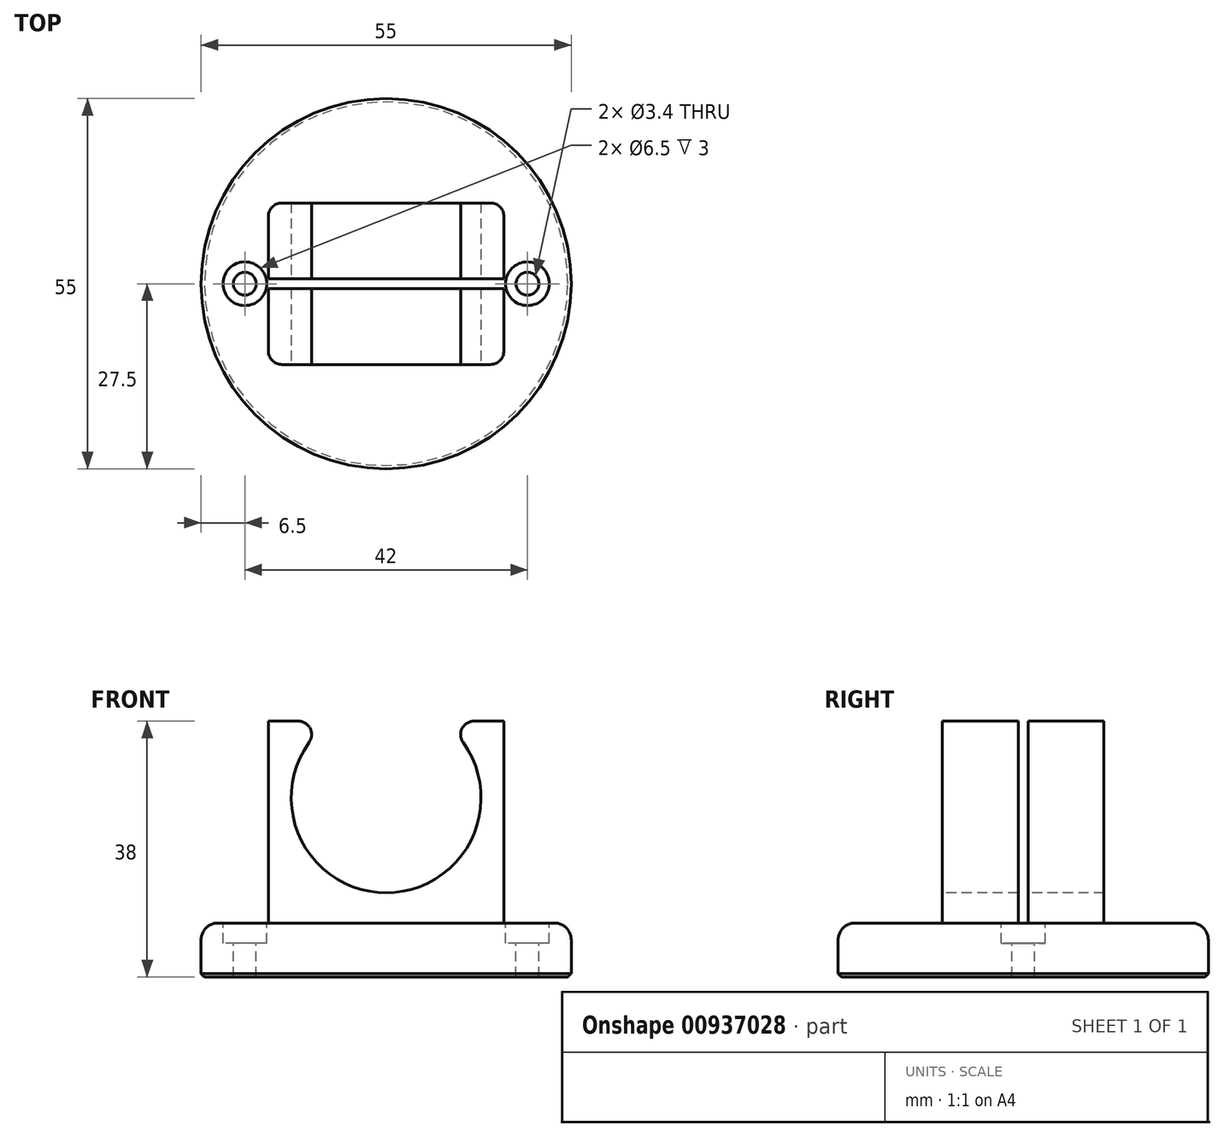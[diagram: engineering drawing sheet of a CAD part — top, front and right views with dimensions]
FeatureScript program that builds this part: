
annotation { "Feature Type Name" : "Feature", "Feature Type Description" : "" }
export const myFeature = defineFeature(function(context is Context, id is Id, definition is map)
    precondition{}
    {
        {
            var Q0;
            Q0=qCreatedBy(makeId("Top.planeOp"),FACE);
            var sketch = newSketch(context, id + "F0", { "sketchPlane" : qUnion([Q0])});
            skCircle(sketch, "E0", {"center": v(0, 0) * mm, "radius": 27.5 * mm});
            skSolve(sketch);
        }
        {
            var Q0;
            Q0 = qSketchRegion(id + "F0", true);
            extrude(context, id + "F1", {"entities" : qUnion([Q0]), "depth" : 8 * mm, "offsetDistance" : 25 * mm});
        }
        {
            var Q0;
            Q0=makeQuery(id+"F1.opExtrude","CAP_FACE",FACE,{"disambiguationData":[OSD([sQuery(id+"F0.wireOp",EDGE,"E0")])],"isStart":false});
            var sketch = newSketch(context, id + "F2", { "sketchPlane" : qUnion([Q0])});
            skLineSegment(sketch, "E1.bottom", {"start": v(17.5, -12) * mm, "end": v(-17.5, -12) * mm});
            skLineSegment(sketch, "E1.top", {"start": v(17.5, 12) * mm, "end": v(-17.5, 12) * mm});
            skLineSegment(sketch, "E1.left", {"start": v(17.5, -12) * mm, "end": v(17.5, 12) * mm});
            skLineSegment(sketch, "E1.right", {"start": v(-17.5, -12) * mm, "end": v(-17.5, 12) * mm});
            skPoint(sketch, "E1.middle", {"position": v(0, 0) * mm});
            skSolve(sketch);
        }
        {
            var Q0;
            Q0 = qSketchRegion(id + "F2", true);
            extrude(context, id + "F3", {"entities" : qUnion([Q0]), "operationType" : NewBodyOperationType.ADD, "depth" : 30 * mm, "offsetDistance" : 25 * mm});
        }
        {
            var Q0;
            Q0=makeQuery(id+"F1.opExtrude","CAP_FACE",FACE,{"disambiguationData":[OSD([sQuery(id+"F0.wireOp",EDGE,"E0")])],"isStart":false});
            var sketch = newSketch(context, id + "F4", { "sketchPlane" : qUnion([Q0])});
            skPoint(sketch, "E2", {"position": v(21, 0) * mm});
            skPoint(sketch, "E3", {"position": v(-21, 0) * mm});
            skSolve(sketch);
        }
        {
            var Q0;
            Q0=makeQuery(id+"F3.opExtrude","SWEPT_FACE",FACE,{"disambiguationData":[OSD([sQuery(id+"F2.wireOp",EDGE,"E1.bottom")])]});
            var sketch = newSketch(context, id + "F5", { "sketchPlane" : qUnion([Q0])});
            skArc(sketch, "E4", {"start": v(-8.2, 38.07) * mm, "mid": v(0, 12.5) * mm, "end": v(8.2, 38.07) * mm});
            skLineSegment(sketch, "E5", {"start": v(-8.2, 38.07) * mm, "end": v(8.2, 38.07) * mm});
            skSolve(sketch);
        }
        {
            var Q0;
            Q0 = qSketchRegion(id + "F5", true);
            extrude(context, id + "F6", {"entities" : qUnion([Q0]), "operationType" : NewBodyOperationType.REMOVE, "oppositeDirection" : true, "depth" : 24 * mm, "offsetDistance" : 25 * mm});
        }
        {
            var Q0;
            Q0=makeQuery(id+"F6.boolean.opBoolean","COPY",EDGE,{"derivedFrom":makeQuery(id+"F6.opExtrude","CAP_EDGE",EDGE,{"disambiguationData":[OSD([sQuery(id+"F5.wireOp",EDGE,"E4")])],"isStart":true})});
            var Q1;
            Q1=makeQuery(id+"F6.boolean.opBoolean","COPY",EDGE,{"derivedFrom":makeQuery(id+"F6.opExtrude","CAP_EDGE",EDGE,{"disambiguationData":[OSD([sQuery(id+"F5.wireOp",EDGE,"E4")])],"isStart":false})});
            var Q2;
            Q2=makeQuery(id+"F3.opExtrude","SWEPT_EDGE",EDGE,{"disambiguationData":[OSD([sQuery(id+"F2.wireOp",EDGE,"E1.bottom"),sQuery(id+"F2.wireOp",EDGE,"E1.left")])]});
            var Q3;
            Q3=makeQuery(id+"F3.opExtrude","SWEPT_EDGE",EDGE,{"disambiguationData":[OSD([sQuery(id+"F2.wireOp",EDGE,"E1.top"),sQuery(id+"F2.wireOp",EDGE,"E1.left")])]});
            var Q4;
            Q4=makeQuery(id+"F3.opExtrude","SWEPT_EDGE",EDGE,{"disambiguationData":[OSD([sQuery(id+"F2.wireOp",EDGE,"E1.top"),sQuery(id+"F2.wireOp",EDGE,"E1.right")])]});
            var Q5;
            Q5=makeQuery(id+"F3.opExtrude","SWEPT_EDGE",EDGE,{"disambiguationData":[OSD([sQuery(id+"F2.wireOp",EDGE,"E1.bottom"),sQuery(id+"F2.wireOp",EDGE,"E1.right")])]});
            fillet(context, id + "F7", {"entities" : qUnion([Q0, Q1, Q2, Q3, Q4, Q5]), "radius" : 2 * mm, "tangentPropagation" : true, "allowEdgeOverflow" : false});
        }
        {
            var Q0;
            Q0=sQuery(id+"F4.wireOp",VERTEX,"E2");
            var Q1;
            Q1=sQuery(id+"F4.wireOp",VERTEX,"E3");
            var Q2;
            Q2=makeQuery(id+"F1.opExtrude","SWEPT_BODY",BODY,{"disambiguationData":[OSD([sQuery(id+"F0.wireOp",EDGE,"E0")])]});
            hole(context, id + "F8", {"style" : HoleStyle.C_BORE, "endStyle" : HoleEndStyle.THROUGH, "standardTappedOrClearance" : lookupTablePath({ "fit" : "Normal", "standard" : "ISO", "size" : "M3", "type" : "Clearance" }), "standardBlindInLast" : lookupTablePath({ "fit" : "Normal", "standard" : "ISO", "engagement" : "75%", "pitch" : "0.5 mm", "size" : "M3", "type" : "Clearance & tapped" }), "holeDiameter" : 3.4 * mm, "cBoreDiameter" : 6.5 * mm, "cBoreDepth" : 3 * mm, "majorDiameter" : 5 * mm, "isTappedThrough" : true, "tappedDepth" : 12 * mm, "tapClearance" : 3, "startFromSketch" : true, "locations" : qUnion([Q0, Q1]), "scope" : qUnion([Q2])});
        }
        {
            var Q0;
            Q0=makeQuery(id+"F1.opExtrude","CAP_EDGE",EDGE,{"disambiguationData":[OSD([sQuery(id+"F0.wireOp",EDGE,"E0")])],"isStart":false});
            fillet(context, id + "F9", {"entities" : qUnion([Q0]), "radius" : 2.5 * mm, "tangentPropagation" : true, "allowEdgeOverflow" : false});
        }
        {
            var Q0;
            {var subQ0=sQuery(id+"F2.wireOp",EDGE,"E1.bottom");var subQ1=sQuery(id+"F2.wireOp",EDGE,"E1.right");var subQ2=sQuery(id+"F2.wireOp",EDGE,"E1.top");Q0=makeQuery(id+"F6.boolean.opBoolean","SPLIT",FACE,{"disambiguationData":[TD([makeQuery(id+"F3.opExtrude","SWEPT_FACE",FACE,{"disambiguationData":[OSD([subQ1])]})])],"derivedFrom":makeQuery(id+"F3.opExtrude","CAP_FACE",FACE,{"disambiguationData":[OSD([subQ0,subQ2,sQuery(id+"F2.wireOp",EDGE,"E1.left"),subQ1])],"isStart":false})});}
            var sketch = newSketch(context, id + "F10", { "sketchPlane" : qUnion([Q0])});
            skLineSegment(sketch, "E6.bottom", {"start": v(17.5, -0.75) * mm, "end": v(-17.5, -0.75) * mm});
            skLineSegment(sketch, "E6.top", {"start": v(17.5, 0.75) * mm, "end": v(-17.5, 0.75) * mm});
            skLineSegment(sketch, "E6.left", {"start": v(17.5, -0.75) * mm, "end": v(17.5, 0.75) * mm});
            skLineSegment(sketch, "E6.right", {"start": v(-17.5, -0.75) * mm, "end": v(-17.5, 0.75) * mm});
            skPoint(sketch, "E6.middle", {"position": v(0, 0) * mm});
            skSolve(sketch);
        }
        {
            var Q0;
            Q0 = qSketchRegion(id + "F10", true);
            extrude(context, id + "F11", {"entities" : qUnion([Q0]), "operationType" : NewBodyOperationType.REMOVE, "oppositeDirection" : true, "depth" : 30 * mm, "offsetDistance" : 25 * mm});
        }
        {
            var Q0;
            Q0=makeQuery(id+"F1.opExtrude","CAP_EDGE",EDGE,{"disambiguationData":[OSD([sQuery(id+"F0.wireOp",EDGE,"E0")])],"isStart":true});
            chamfer(context, id + "F12", {"entities" : qUnion([Q0]), "width" : .5 * mm, "tangentPropagation" : true});
        }
        {
            var Q0;
            {var subQ0=makeQuery(id+"F3.opExtrude","CAP_FACE",FACE,{"disambiguationData":[OSD([sQuery(id+"F2.wireOp",EDGE,"E1.bottom"),sQuery(id+"F2.wireOp",EDGE,"E1.top"),sQuery(id+"F2.wireOp",EDGE,"E1.left"),sQuery(id+"F2.wireOp",EDGE,"E1.right")])],"isStart":false});var subQ1=sQuery(id+"F5.wireOp",EDGE,"E4");var subQ2=makeQuery(id+"F6.opExtrude","SWEPT_FACE",FACE,{"disambiguationData":[OSD([subQ1])]});Q0=makeQuery(id+"F11.boolean.opBoolean","SPLIT",EDGE,{"disambiguationData":[TD([makeQuery(id+"F11.opExtrude","SWEPT_FACE",FACE,{"disambiguationData":[OSD([sQuery(id+"F10.wireOp",EDGE,"E6.bottom")])]})])],"derivedFrom":makeQuery(id+"F6.boolean.opBoolean","INTERSECT",EDGE,{"disambiguationData":[OD(1.0)],"derivedFrom":[subQ0,subQ2]})});}
            var Q1;
            {var subQ0=makeQuery(id+"F3.opExtrude","CAP_FACE",FACE,{"disambiguationData":[OSD([sQuery(id+"F2.wireOp",EDGE,"E1.bottom"),sQuery(id+"F2.wireOp",EDGE,"E1.top"),sQuery(id+"F2.wireOp",EDGE,"E1.left"),sQuery(id+"F2.wireOp",EDGE,"E1.right")])],"isStart":false});var subQ1=sQuery(id+"F5.wireOp",EDGE,"E4");var subQ2=makeQuery(id+"F6.opExtrude","SWEPT_FACE",FACE,{"disambiguationData":[OSD([subQ1])]});Q1=makeQuery(id+"F11.boolean.opBoolean","SPLIT",EDGE,{"disambiguationData":[TD([makeQuery(id+"F11.opExtrude","SWEPT_FACE",FACE,{"disambiguationData":[OSD([sQuery(id+"F10.wireOp",EDGE,"E6.top")])]})])],"derivedFrom":makeQuery(id+"F6.boolean.opBoolean","INTERSECT",EDGE,{"disambiguationData":[OD(1.0)],"derivedFrom":[subQ0,subQ2]})});}
            var Q2;
            {var subQ0=makeQuery(id+"F3.opExtrude","CAP_FACE",FACE,{"disambiguationData":[OSD([sQuery(id+"F2.wireOp",EDGE,"E1.bottom"),sQuery(id+"F2.wireOp",EDGE,"E1.top"),sQuery(id+"F2.wireOp",EDGE,"E1.left"),sQuery(id+"F2.wireOp",EDGE,"E1.right")])],"isStart":false});var subQ1=sQuery(id+"F5.wireOp",EDGE,"E4");var subQ2=makeQuery(id+"F6.opExtrude","SWEPT_FACE",FACE,{"disambiguationData":[OSD([subQ1])]});Q2=makeQuery(id+"F11.boolean.opBoolean","SPLIT",EDGE,{"disambiguationData":[TD([makeQuery(id+"F11.opExtrude","SWEPT_FACE",FACE,{"disambiguationData":[OSD([sQuery(id+"F10.wireOp",EDGE,"E6.bottom")])]})])],"derivedFrom":makeQuery(id+"F6.boolean.opBoolean","INTERSECT",EDGE,{"disambiguationData":[OD(0.0)],"derivedFrom":[subQ0,subQ2]})});}
            var Q3;
            {var subQ0=makeQuery(id+"F3.opExtrude","CAP_FACE",FACE,{"disambiguationData":[OSD([sQuery(id+"F2.wireOp",EDGE,"E1.bottom"),sQuery(id+"F2.wireOp",EDGE,"E1.top"),sQuery(id+"F2.wireOp",EDGE,"E1.left"),sQuery(id+"F2.wireOp",EDGE,"E1.right")])],"isStart":false});var subQ1=sQuery(id+"F5.wireOp",EDGE,"E4");var subQ2=makeQuery(id+"F6.opExtrude","SWEPT_FACE",FACE,{"disambiguationData":[OSD([subQ1])]});Q3=makeQuery(id+"F11.boolean.opBoolean","SPLIT",EDGE,{"disambiguationData":[TD([makeQuery(id+"F11.opExtrude","SWEPT_FACE",FACE,{"disambiguationData":[OSD([sQuery(id+"F10.wireOp",EDGE,"E6.top")])]})])],"derivedFrom":makeQuery(id+"F6.boolean.opBoolean","INTERSECT",EDGE,{"disambiguationData":[OD(0.0)],"derivedFrom":[subQ0,subQ2]})});}
            fillet(context, id + "F13", {"entities" : qUnion([Q0, Q1, Q2, Q3]), "radius" : 2 * mm, "tangentPropagation" : true, "allowEdgeOverflow" : false});
        }
    });
